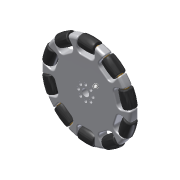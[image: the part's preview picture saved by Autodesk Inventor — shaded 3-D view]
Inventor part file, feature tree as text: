
AUTODESK INVENTOR PART (.ipt)
format: ipt  version: 2013 (Build 170138000, 138)  size: 783,872 bytes
history: native  units: in
note: dims shown in document units (in); Inventor stores cm internally (conversion verified against a paired STEP export)
features: sketch x6, extrude x4, fillet x4, other x3, pattern_circular x3, plane x1, revolve x1, projected_geometry x1
ambient origin geometry x8: Origin, YZ Plane, XZ Plane, XY Plane, X Axis, Y Axis, Z Axis, Center Point
feature tree (23):
  other  "Hub"
  extrude  "Extrusion1"  Depth=0.3937in TaperAngle=0.0deg
  fillet  "Fillet1"  Radius=0.125in
  extrude  "Extrusion2"  Depth=0.1875in
  plane  "Work Plane1"
  sketch  "Sketch4"  dims[d7=1.35in d9=2.0in d10=0.3937in d11=0.0in d16=1.7435in]
  revolve  "Revolution1"  [1 undecoded]
  fillet  "Fillet2"  Radius=0.3937in
  fillet  "Fillet3"  Radius=1.7435in
  extrude  "Extrusion3"  Depth=1.7435in
  pattern_circular  "Circular Pattern2"  Angle=90.0deg  [1 undecoded]
  fillet  "Fillet4"  Radius=0.05in
  pattern_circular  "Circular Pattern3"  [2 undecoded]
  pattern_circular  "Circular Pattern4"  [2 undecoded]
  extrude  "Extrusion4"  Depth=0.75in
  sketch  "Sketch1"  dims[d0=3.9in d1=0.3937in d2=0.0in d3=0.125in]
  sketch  "Sketch2"  dims[d4=0.1875in d6=0.1875in]
  projected_geometry  "Projected Loop1"
  sketch  "Sketch5"  dims[d17=0.69in d19=1.7435in]
  other  "Rollers"
  sketch  "Sketch6"  dims[d20=0.2309in]
  other  "Bearing"
  sketch  "Sketch7"  dims[d21=0.2565in d22=90.0deg d23=0.05in d24=0.05in d25=0.25in d26=0.75in d27=0.0in d29=3.937in d30=360.0deg d32=0.05in d33=3.937in d34=360.0deg d36=3.937in d37=360.0deg d39=0.315in d40=0.1457in d41=0.6299in d42=3.1496in d44=360.0deg d46=0.75in d47=0.0in d49=0.0in d50=0.0in]
note: 6 required parameter values undecoded (feature->parameter linkage not recoverable at this tier; creation-order binding heuristic only, values carry confidence <= 0.55)